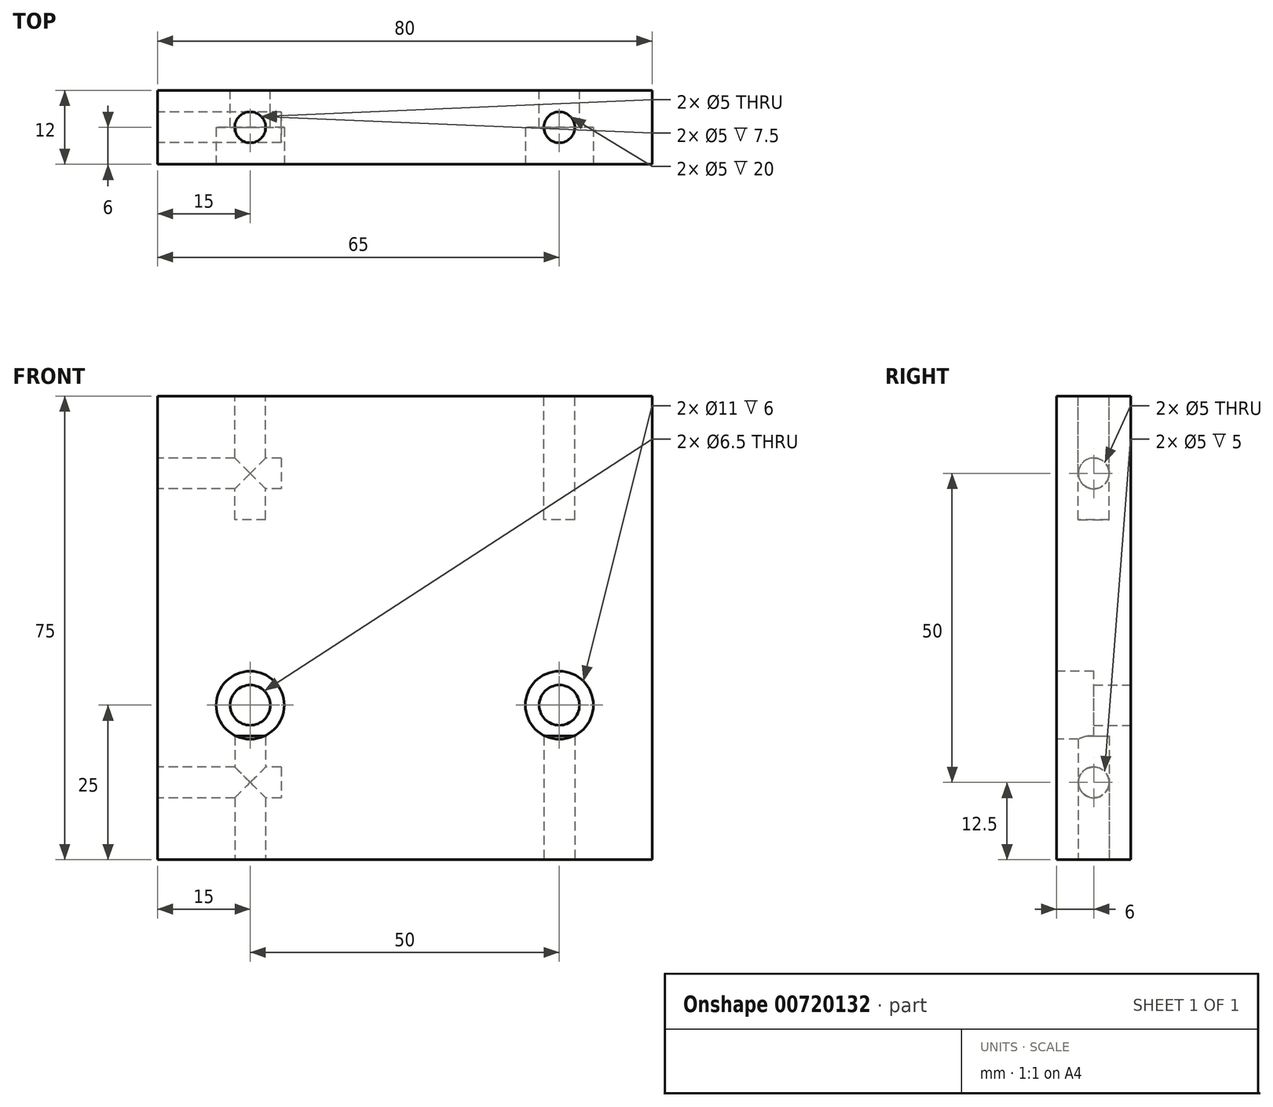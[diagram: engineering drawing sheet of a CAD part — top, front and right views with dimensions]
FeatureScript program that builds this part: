
annotation { "Feature Type Name" : "Feature", "Feature Type Description" : "" }
export const myFeature = defineFeature(function(context is Context, id is Id, definition is map)
    precondition{}
    {
        {
            var Q0;
            Q0=qCreatedBy(makeId("Front.planeOp"),FACE);
            var sketch = newSketch(context, id + "F0", { "sketchPlane" : qUnion([Q0])});
            skLineSegment(sketch, "E0.bottom", {"start": v(0, 0) * mm, "end": v(80, 0) * mm});
            skLineSegment(sketch, "E0.top", {"start": v(0, 75) * mm, "end": v(80, 75) * mm});
            skLineSegment(sketch, "E0.left", {"start": v(0, 0) * mm, "end": v(0, 75) * mm});
            skLineSegment(sketch, "E0.right", {"start": v(80, 0) * mm, "end": v(80, 75) * mm});
            skCircle(sketch, "E1", {"center": v(15, 25) * mm, "radius": 3.25 * mm});
            skCircle(sketch, "E2", {"center": v(65, 25) * mm, "radius": 3.25 * mm});
            skSolve(sketch);
        }
        {
            var Q0;
            Q0=makeQuery(id+"F0.imprint","IMPRINT",FACE,{"disambiguationData":[TD([[makeQuery(id+"F0.imprint","IMPRINT",EDGE,{"derivedFrom":sQuery(id+"F0.wireOp",EDGE,"E0.bottom")}),1.0]])]});
            extrude(context, id + "F1", {"entities" : qUnion([Q0]), "depth" : 12 * mm, "offsetDistance" : 25 * mm});
        }
        {
            var Q0;
            Q0=makeQuery(id+"F1.opExtrude","CAP_FACE",FACE,{"disambiguationData":[OSD([sQuery(id+"F0.wireOp",EDGE,"E0.bottom"),sQuery(id+"F0.wireOp",EDGE,"E0.top"),sQuery(id+"F0.wireOp",EDGE,"E0.left"),sQuery(id+"F0.wireOp",EDGE,"E0.right"),sQuery(id+"F0.wireOp",EDGE,"E1"),sQuery(id+"F0.wireOp",EDGE,"E2")])],"isStart":false});
            var sketch = newSketch(context, id + "F2", { "sketchPlane" : qUnion([Q0])});
            skCircle(sketch, "E3", {"center": v(15, 25) * mm, "radius": 5.5 * mm});
            skCircle(sketch, "E4", {"center": v(65, 25) * mm, "radius": 5.5 * mm});
            skSolve(sketch);
        }
        {
            var Q0;
            Q0 = qSketchRegion(id + "F2", true);
            extrude(context, id + "F3", {"entities" : qUnion([Q0]), "operationType" : NewBodyOperationType.REMOVE, "oppositeDirection" : true, "depth" : 6 * mm, "offsetDistance" : 25 * mm});
        }
        {
            var Q0;
            Q0=makeQuery(id+"F1.opExtrude","SWEPT_FACE",FACE,{"disambiguationData":[OSD([sQuery(id+"F0.wireOp",EDGE,"E0.bottom")])]});
            var sketch = newSketch(context, id + "F4", { "sketchPlane" : qUnion([Q0])});
            skCircle(sketch, "E5", {"center": v(15, 6) * mm, "radius": 2.5 * mm});
            skPoint(sketch, "E5.centerSnap0", {"position": v(0, 6) * mm});
            skCircle(sketch, "E6", {"center": v(65, 6) * mm, "radius": 2.5 * mm});
            skSolve(sketch);
        }
        {
            var Q0;
            Q0=makeQuery(id+"F4.imprint","IMPRINT",FACE,{"disambiguationData":[TD([[makeQuery(id+"F4.imprint","IMPRINT",EDGE,{"derivedFrom":sQuery(id+"F4.wireOp",EDGE,"E5")}),1.0]])]});
            var Q1;
            Q1=makeQuery(id+"F4.imprint","IMPRINT",FACE,{"disambiguationData":[TD([[makeQuery(id+"F4.imprint","IMPRINT",EDGE,{"derivedFrom":sQuery(id+"F4.wireOp",EDGE,"E6")}),1.0]])]});
            extrude(context, id + "F5", {"entities" : qUnion([Q0, Q1]), "operationType" : NewBodyOperationType.REMOVE, "oppositeDirection" : true, "depth" : 20 * mm, "offsetDistance" : 25 * mm});
        }
        {
            var Q0;
            Q0=makeQuery(id+"F1.opExtrude","SWEPT_FACE",FACE,{"disambiguationData":[OSD([sQuery(id+"F0.wireOp",EDGE,"E0.top")])]});
            var sketch = newSketch(context, id + "F6", { "sketchPlane" : qUnion([Q0])});
            skCircle(sketch, "E7", {"center": v(15, -6) * mm, "radius": 2.5 * mm});
            skCircle(sketch, "E8", {"center": v(65, -6) * mm, "radius": 2.5 * mm});
            skSolve(sketch);
        }
        {
            var Q0;
            Q0=makeQuery(id+"F6.imprint","IMPRINT",FACE,{"disambiguationData":[TD([[makeQuery(id+"F6.imprint","IMPRINT",EDGE,{"derivedFrom":sQuery(id+"F6.wireOp",EDGE,"E7")}),1.0]])]});
            var Q1;
            Q1=makeQuery(id+"F6.imprint","IMPRINT",FACE,{"disambiguationData":[TD([[makeQuery(id+"F6.imprint","IMPRINT",EDGE,{"derivedFrom":sQuery(id+"F6.wireOp",EDGE,"E8")}),1.0]])]});
            extrude(context, id + "F7", {"entities" : qUnion([Q0, Q1]), "operationType" : NewBodyOperationType.REMOVE, "oppositeDirection" : true, "depth" : 20 * mm, "offsetDistance" : 25 * mm});
        }
        {
            var Q0;
            Q0=makeQuery(id+"F1.opExtrude","SWEPT_FACE",FACE,{"disambiguationData":[OSD([sQuery(id+"F0.wireOp",EDGE,"E0.left")])]});
            var sketch = newSketch(context, id + "F8", { "sketchPlane" : qUnion([Q0])});
            skCircle(sketch, "E9", {"center": v(6, 62.5) * mm, "radius": 2.5 * mm});
            skPoint(sketch, "E9.centerSnap0", {"position": v(6, 75) * mm});
            skCircle(sketch, "E10", {"center": v(6, 12.5) * mm, "radius": 2.5 * mm});
            skSolve(sketch);
        }
        {
            var Q0;
            Q0 = qSketchRegion(id + "F8", true);
            extrude(context, id + "F9", {"entities" : qUnion([Q0]), "operationType" : NewBodyOperationType.REMOVE, "oppositeDirection" : true, "depth" : 20 * mm, "offsetDistance" : 25 * mm});
        }
    });
